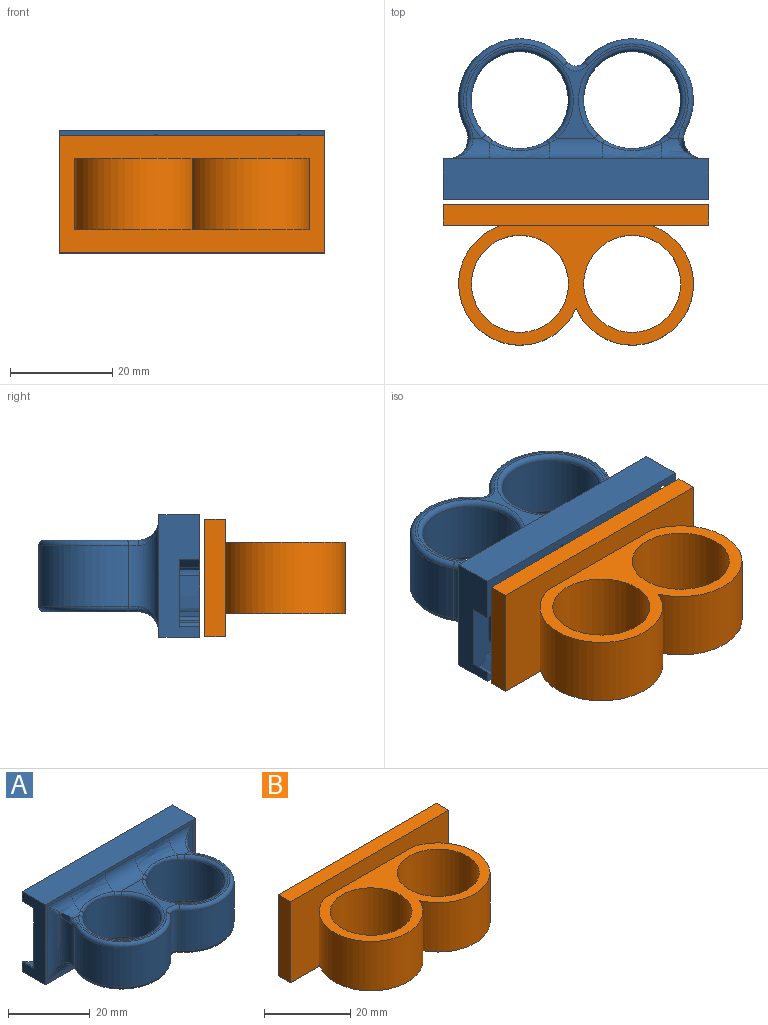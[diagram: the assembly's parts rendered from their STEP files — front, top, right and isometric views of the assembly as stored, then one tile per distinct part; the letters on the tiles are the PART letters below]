
ASSEMBLY  parts=2 mates=1
PART A: 139 faces, bbox 52.1x32.5x24 mm
  f0: plane 52.1x24mm, normal (0,1,0), area 576.6mm2, adj f1,f10,f11,f12,f13,f14,f15,f16
  f1: extruded ~4x0.86mm, area 4.6mm2, adj f0,f2,f10,f94
  f2: plane 17.06x11.58mm, normal (0,1,0), area 139mm2, adj f1,f3,f5,f6,f7,f8,f9,f10
  f3: extruded ~4x3.6mm, area 16.4mm2, adj f2,f4,f5,f9
  f4: plane 8.19x2.91mm, normal (0,1,0), area 19.6mm2, adj f3,f5,f6,f7,f8,f9
  f5: extruded ~4x2.87mm, area 11.5mm2, adj f2,f3,f4,f6
  f6: extruded ~4x1.33mm, area 5.8mm2, adj f2,f4,f5,f7
  f7: extruded ~4x2.3mm, area 10.4mm2, adj f2,f4,f6,f8
  f8: extruded ~7.11x4mm, area 28.9mm2, adj f2,f4,f7,f9
  f9: extruded ~4x0.84mm, area 3.8mm2, adj f2,f3,f4,f8
  f10: extruded ~4x2.76mm, area 15mm2, adj f0,f1,f2,f11
  f11: extruded ~4x2.68mm, area 13.6mm2, adj f0,f2,f10,f12
  f12: extruded ~4.67x4mm, area 22.4mm2, adj f0,f2,f11,f13
  f13: extruded ~4x0.61mm, area 2.8mm2, adj f0,f2,f12,f14
  f14: extruded ~8.65x4mm, area 34.7mm2, adj f0,f2,f13,f15
  f15: extruded ~4x0.99mm, area 5.7mm2, adj f0,f2,f14,f16
  f16: extruded ~4.97x4.06mm, area 25.7mm2, adj f0,f2,f15,f17
  f17: extruded ~4x3.6mm, area 15.8mm2, adj f0,f2,f16,f18
  f18: extruded ~4x1.92mm, area 8.6mm2, adj f0,f2,f17,f93
  f19: plane 52x8mm, normal (0,0,1), area 416mm2, adj f0,f20,f91,f93
  f20: plane 52x24mm, normal (0,-1,0), area 154.8mm2, adj f19,f21,f60,f61,f62,f63,f64,f65
  f21: cylinder r=4mm len=8.3mm, axis (1,0,0), area 31.4mm2, adj f20,f22,f57,f58,f59,f60
  f22: plane 44x18.5mm, normal (0,0,-1), area 72.4mm2, adj f21,f23,f24,f51,f52,f53,f55,f56
  f23: torus R=5mm, axis (0,0,1), area 3.3mm2, adj f22,f24,f57,f71
  f24: torus R=11mm, axis (0,0,1), area 54.2mm2, adj f22,f23,f25,f51
  f25: cylinder r=12mm len=21.43mm, axis (0,0,-1), area 426.6mm2, adj f24,f26,f50,f71
  f26: torus R=11mm, axis (0,0,1), area 54.2mm2, adj f25,f27,f29,f49
  f27: torus R=5mm, axis (0,0,1), area 3.3mm2, adj f26,f28,f29,f71
  f28: bspline ~3.31x2.56mm, area 2.3mm2, adj f27,f69,f71
  f29: plane 44x18.5mm, normal (0,0,1), area 72.4mm2, adj f26,f27,f30,f38,f40,f42,f49,f65
  f30: torus R=10.5mm, axis (0,0,1), area 73.3mm2, adj f29,f31,f33,f37
  f31: bspline ~3.9x3.1mm, area 2.6mm2, adj f30,f32,f33,f67
  f32: bspline ~12.34x2.31mm, area 12.3mm2, adj f31,f33,f37,f66
  f33: cylinder r=9.5mm len=19mm, axis (0,0,-1), area 720.3mm2, adj f30,f31,f32,f34,f35,f36,f37,f55
  f34: bspline ~3.9x3.1mm, area 2.6mm2, adj f33,f35,f55,f61
  f35: bspline ~12.62x2.4mm, area 12.3mm2, adj f33,f34,f36,f62
  f36: bspline ~3.9x3.1mm, area 2.6mm2, adj f33,f35,f55,f63
  f37: bspline ~3.9x3.1mm, area 2.6mm2, adj f30,f32,f33,f65
  f38: torus R=5mm, axis (0,0,1), area 3.3mm2, adj f29,f39,f40,f64
  f39: bspline ~5x5mm, area 4.3mm2, adj f38,f64,f65
  f40: torus R=11mm, axis (0,0,1), area 54.2mm2, adj f29,f38,f41,f49
  f41: cylinder r=12mm len=21.43mm, axis (0,0,-1), area 426.6mm2, adj f40,f50,f52,f64
  f42: torus R=10.5mm, axis (0,0,1), area 73.3mm2, adj f29,f43,f47,f48
  f43: cylinder r=9.5mm len=19mm, axis (0,0,-1), area 720.3mm2, adj f42,f44,f45,f46,f47,f48,f56,f59
  f44: bspline ~12.14x2.31mm, area 12.3mm2, adj f43,f45,f59,f60
  f45: bspline ~3.9x3.1mm, area 2.6mm2, adj f43,f44,f56,f61
  f46: bspline ~12.62x2.4mm, area 12.3mm2, adj f43,f47,f48,f68
  f47: bspline ~3.9x3.1mm, area 2.6mm2, adj f42,f43,f46,f67
  f48: bspline ~3.9x3.1mm, area 2.6mm2, adj f42,f43,f46,f69
  f49: torus R=3mm, axis (0,0,1), area 6.7mm2, adj f26,f29,f40,f50
  f50: cylinder r=2mm len=12mm, axis (0,0,1), area 43.4mm2, adj f25,f41,f49,f51
  f51: torus R=3mm, axis (0,0,1), area 6.7mm2, adj f22,f24,f50,f52
  f52: torus R=11mm, axis (0,0,1), area 54.2mm2, adj f22,f41,f51,f53
  f53: torus R=5mm, axis (0,0,1), area 3.3mm2, adj f22,f52,f54,f64
  f54: bspline ~5x5mm, area 4.3mm2, adj f53,f63,f64
  f55: torus R=10.5mm, axis (0,0,1), area 73.3mm2, adj f22,f33,f34,f36
  f56: torus R=10.5mm, axis (0,0,1), area 73.3mm2, adj f22,f43,f45,f59
  f57: bspline ~3.31x2.56mm, area 2.3mm2, adj f21,f23,f71
  f58: bspline ~3.65x3.65mm, area 0.9mm2, adj f21,f71
  f59: bspline ~3.9x3.1mm, area 2.6mm2, adj f21,f43,f44,f56
  f60: bspline ~14x4.71mm, area 48mm2, adj f20,f21,f44,f61
  f61: cylinder r=4mm len=10.34mm, axis (1,0,0), area 63.4mm2, adj f20,f22,f34,f45,f60,f62
  f62: bspline ~14x4.71mm, area 48mm2, adj f20,f35,f61,f63
  f63: cylinder r=4mm len=8.3mm, axis (1,0,0), area 31.4mm2, adj f20,f22,f36,f54,f62
  f64: cylinder r=4mm len=22mm, axis (0,0,-1), area 121.6mm2, adj f20,f38,f39,f41,f53,f54
  f65: cylinder r=4mm len=8.3mm, axis (-1,0,0), area 31.4mm2, adj f20,f29,f37,f39,f66
  f66: bspline ~14.64x4.91mm, area 48mm2, adj f20,f32,f65,f67
  f67: cylinder r=4mm len=10.34mm, axis (-1,0,0), area 63.4mm2, adj f20,f29,f31,f47,f66,f68
  f68: bspline ~14.64x4.91mm, area 48mm2, adj f20,f46,f67,f69
  f69: cylinder r=4mm len=8.3mm, axis (-1,0,0), area 31.4mm2, adj f20,f28,f29,f48,f68,f70
  f70: bspline ~3.65x3.65mm, area 0.9mm2, adj f69,f71
  f71: cylinder r=4mm len=22mm, axis (0,0,-1), area 121.6mm2, adj f20,f23,f25,f27,f28,f57,f58,f70
  f72: extruded ~4.22x4mm, area 18.5mm2, adj f0,f73,f81,f91
  f73: plane 22.87x11.26mm, normal (0,1,0), area 149.7mm2, adj f72,f74,f76,f77,f78,f79,f80,f81
  f74: extruded ~4x2.68mm, area 12.8mm2, adj f73,f75,f76,f80
  f75: plane 7.64x3.58mm, normal (0,1,0), area 19mm2, adj f74,f76,f77,f78,f79,f80
  f76: extruded ~4x2.54mm, area 11.5mm2, adj f73,f74,f75,f77
  f77: extruded ~4x3.58mm, area 14.3mm2, adj f73,f75,f76,f78
  f78: extruded ~4x0.91mm, area 4.8mm2, adj f73,f75,f77,f79
  f79: extruded ~6.5x4mm, area 33.8mm2, adj f73,f75,f78,f80
  f80: extruded ~4x0.3mm, area 1.2mm2, adj f73,f74,f75,f79
  f81: extruded ~4x1.15mm, area 4.8mm2, adj f0,f72,f73,f82
  f82: plane 4x0.3mm, normal (-0.79,0,-0.62), area 1.5mm2, adj f0,f73,f81,f83
  f83: extruded ~4x1.07mm, area 5.5mm2, adj f0,f73,f82,f84
  f84: extruded ~6.89x4mm, area 39mm2, adj f0,f73,f83,f85
  f85: extruded ~4x1mm, area 5.2mm2, adj f0,f73,f84,f86
  f86: extruded ~4x3.98mm, area 20.2mm2, adj f0,f73,f85,f87
  f87: extruded ~5.35x4mm, area 22.2mm2, adj f0,f73,f86,f88
  f88: extruded ~6.36x4.35mm, area 31mm2, adj f0,f73,f87,f89
  f89: extruded ~5.97x4mm, area 27.9mm2, adj f0,f73,f88,f90
  f90: extruded ~4x0.86mm, area 4.1mm2, adj f0,f73,f89,f91
  f91: plane 24x8mm, normal (-1,0,0), area 119.5mm2, adj f0,f19,f20,f72,f73,f90,f92
  f92: plane 52x8mm, normal (0,0,-1), area 416mm2, adj f0,f20,f91,f93
  f93: plane 24x8mm, normal (1,0,0), area 140mm2, adj f0,f2,f18,f19,f20,f92,f94
  f94: extruded ~4x0.4mm, area 2.2mm2, adj f0,f1,f2,f93
  f95: extruded ~4x3.14mm, area 15.6mm2, adj f0,f96,f104,f117
  f96: plane 17.06x13.23mm, normal (0,1,0), area 145.6mm2, adj f95,f97,f99,f100,f101,f102,f103,f104
  f97: extruded ~4x3.6mm, area 16.4mm2, adj f96,f98,f99,f103
  f98: plane 8.19x2.91mm, normal (0,1,0), area 19.6mm2, adj f97,f99,f100,f101,f102,f103
  f99: extruded ~4x2.87mm, area 11.5mm2, adj f96,f97,f98,f100
  f100: extruded ~4x1.33mm, area 5.8mm2, adj f96,f98,f99,f101
  f101: extruded ~4x2.3mm, area 10.4mm2, adj f96,f98,f100,f102
  f102: extruded ~7.11x4mm, area 28.9mm2, adj f96,f98,f101,f103
  f103: extruded ~4x0.84mm, area 3.8mm2, adj f96,f97,f98,f102
  f104: extruded ~4x0.86mm, area 4.6mm2, adj f0,f95,f96,f105
  f105: extruded ~4x2.76mm, area 15mm2, adj f0,f96,f104,f106
  f106: extruded ~4x2.68mm, area 13.6mm2, adj f0,f96,f105,f107
  f107: extruded ~4.67x4mm, area 22.4mm2, adj f0,f96,f106,f108
  f108: extruded ~4x0.61mm, area 2.8mm2, adj f0,f96,f107,f109
  f109: extruded ~8.65x4mm, area 34.7mm2, adj f0,f96,f108,f110
  f110: extruded ~4x0.99mm, area 5.7mm2, adj f0,f96,f109,f111
  f111: extruded ~4.97x4.06mm, area 25.7mm2, adj f0,f96,f110,f112
  f112: extruded ~4x3.6mm, area 15.8mm2, adj f0,f96,f111,f113
  f113: extruded ~4x3.14mm, area 14.4mm2, adj f0,f96,f112,f114
  f114: extruded ~4x1.69mm, area 8mm2, adj f0,f96,f113,f115
  f115: extruded ~4x1.6mm, area 6.4mm2, adj f0,f96,f114,f116
  f116: extruded ~5.59x4mm, area 22.9mm2, adj f0,f96,f115,f117
  f117: extruded ~4x0.84mm, area 4.5mm2, adj f0,f95,f96,f116
  f118: extruded ~4x1.07mm, area 5.5mm2, adj f0,f119,f127,f138
  f119: plane 22.87x12.16mm, normal (0,1,0), area 156.6mm2, adj f118,f120,f122,f123,f124,f125,f126,f127
  f120: extruded ~4x2.68mm, area 12.8mm2, adj f119,f121,f122,f126
  f121: plane 7.64x3.58mm, normal (0,1,0), area 19mm2, adj f120,f122,f123,f124,f125,f126
  f122: extruded ~4x2.54mm, area 11.5mm2, adj f119,f120,f121,f123
  f123: extruded ~4x3.58mm, area 14.3mm2, adj f119,f121,f122,f124
  f124: extruded ~4x0.91mm, area 4.8mm2, adj f119,f121,f123,f125
  f125: extruded ~6.5x4mm, area 33.8mm2, adj f119,f121,f124,f126
  f126: extruded ~4x0.3mm, area 1.2mm2, adj f119,f120,f121,f125
  f127: extruded ~6.89x4mm, area 39mm2, adj f0,f118,f119,f128
  f128: extruded ~4x1mm, area 5.2mm2, adj f0,f119,f127,f129
  f129: extruded ~4x3.98mm, area 20.2mm2, adj f0,f119,f128,f130
  f130: extruded ~5.35x4mm, area 22.2mm2, adj f0,f119,f129,f131
  f131: extruded ~6.36x4.35mm, area 31mm2, adj f0,f119,f130,f132
  f132: extruded ~5.97x4mm, area 27.9mm2, adj f0,f119,f131,f133
  f133: extruded ~4x1.84mm, area 8.8mm2, adj f0,f119,f132,f134
  f134: extruded ~4x1.3mm, area 5.9mm2, adj f0,f119,f133,f135
  f135: extruded ~15x4mm, area 60.4mm2, adj f0,f119,f134,f136
  f136: extruded ~5.2x4mm, area 25.3mm2, adj f0,f119,f135,f137
  f137: extruded ~4x1.15mm, area 4.8mm2, adj f0,f119,f136,f138
  f138: plane 4x0.3mm, normal (-0.79,0,-0.62), area 1.5mm2, adj f0,f118,f119,f137
PART B: 12 faces, bbox 52x27.5x23 mm
  f0: plane 52x23mm, normal (0,-1,0), area 792mm2, adj f1,f3,f4,f5,f6,f8,f10,f11
  f1: plane 23x4mm, normal (1,0,0), area 92mm2, adj f0,f2,f4,f5
  f2: plane 52x23mm, normal (0,1,0), area 1196mm2, adj f1,f3,f4,f5
  f3: plane 23x4mm, normal (-1,0,0), area 92mm2, adj f0,f2,f4,f5
  f4: plane 52x4mm, normal (0,0,1), area 208mm2, adj f0,f1,f2,f3
  f5: plane 52x4mm, normal (0,0,-1), area 208mm2, adj f0,f1,f2,f3
  f6: cylinder r=12mm len=23.5mm, axis (0,0,-1), area 673.9mm2, adj f0,f8,f10,f11
  f7: cylinder r=9.5mm len=19mm, axis (0,0,-1), area 835.7mm2, adj f10,f11
  f8: cylinder r=12mm len=23.5mm, axis (0,0,-1), area 673.9mm2, adj f0,f6,f10,f11
  f9: cylinder r=9.5mm len=19mm, axis (0,0,-1), area 835.7mm2, adj f10,f11
  f10: plane 46x23.5mm, normal (0,0,1), area 355.8mm2, adj f0,f6,f7,f8,f9
  f11: plane 46x23.5mm, normal (0,0,-1), area 355.8mm2, adj f0,f6,f7,f8,f9
PLACE A rot(axis=(0,0,-1),180deg) t=(-55,50.72,-3.2)mm
PLACE B t=(-54.96,-25.28,-3.61)mm
MATE parallel B.f2 <-> A.f2  axis (0,1,0) through (-54.96,10.22,-3.61)mm
